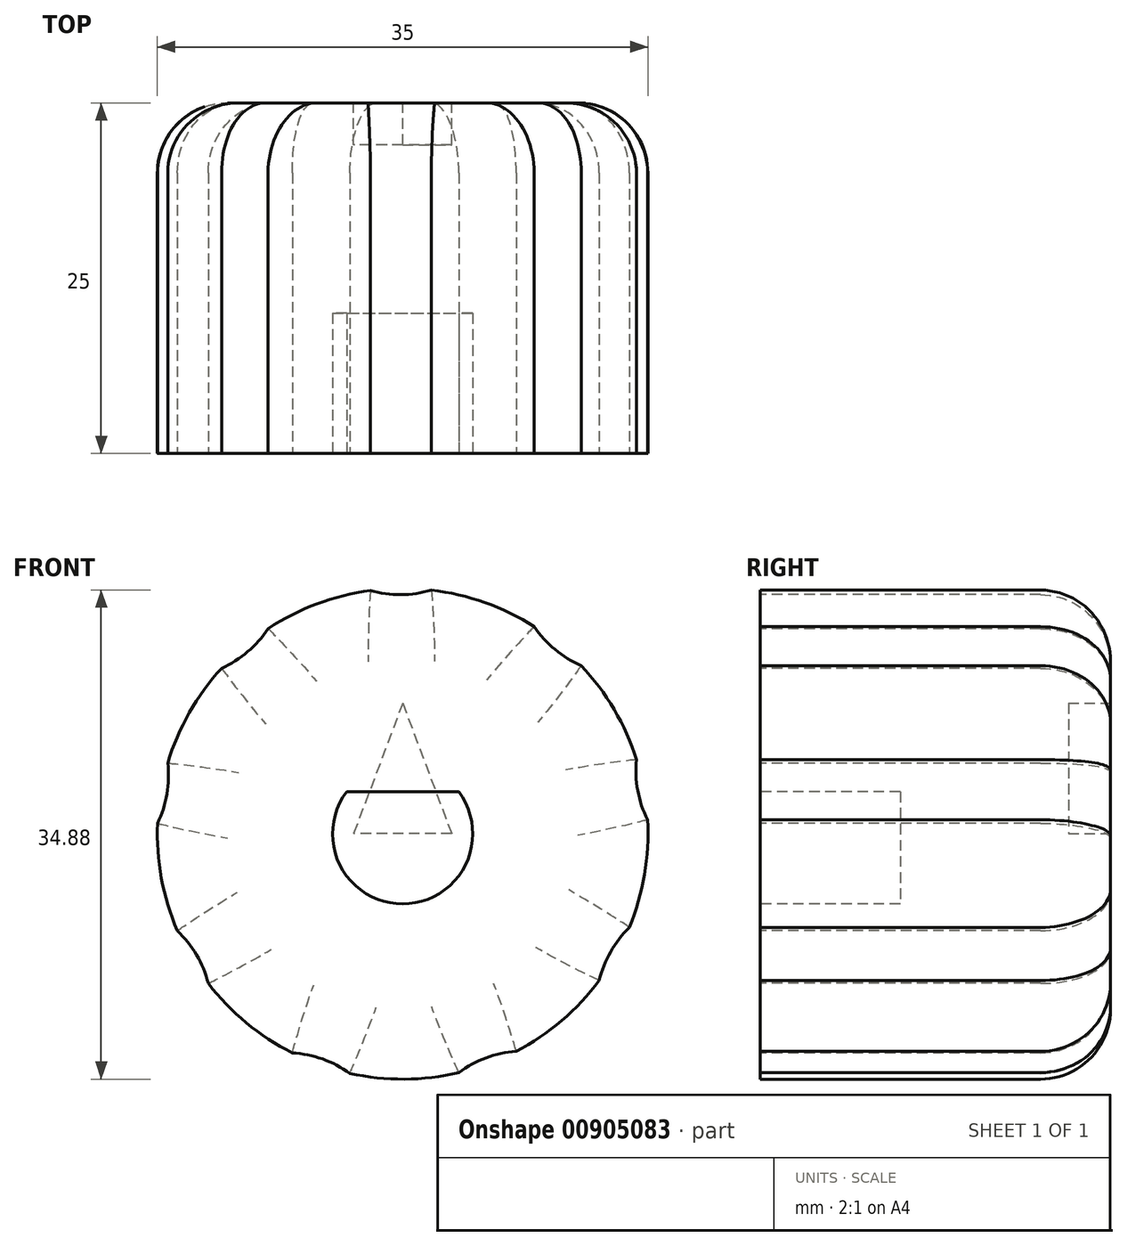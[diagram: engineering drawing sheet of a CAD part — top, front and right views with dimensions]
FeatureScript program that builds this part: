
annotation { "Feature Type Name" : "Feature", "Feature Type Description" : "" }
export const myFeature = defineFeature(function(context is Context, id is Id, definition is map)
    precondition{}
    {
        {
            var Q0;
            Q0=qCreatedBy(makeId("Front.planeOp"),FACE);
            var sketch = newSketch(context, id + "F0", { "sketchPlane" : qUnion([Q0])});
            skCircle(sketch, "E0", {"center": v(0, 0) * mm, "radius": 17.5 * mm});
            skCircle(sketch, "E1", {"center": v(0, 0) * mm, "radius": 5 * mm});
            skLineSegment(sketch, "E2", {"start": v(-4, 3) * mm, "end": v(4, 3) * mm});
            skLineSegment(sketch, "E3", {"start": v(-2.3, 17.35) * mm, "end": v(2.05, 17.38) * mm, "construction": true});
            skArc(sketch, "E4", {"start": v(-2.3, 17.35) * mm, "mid": v(-0.12, 17.05) * mm, "end": v(2.05, 17.38) * mm});
            skArc(sketch, "E5.1.0", {"start": v(-12.92, 11.8) * mm, "mid": v(-11.06, 12.98) * mm, "end": v(-9.6, 14.63) * mm});
            skArc(sketch, "E5.2.0", {"start": v(-17.48, 0.74) * mm, "mid": v(-16.82, 2.84) * mm, "end": v(-16.76, 5.04) * mm});
            skArc(sketch, "E5.3.0", {"start": v(-13.87, -10.67) * mm, "mid": v(-14.7, -8.63) * mm, "end": v(-16.08, -6.91) * mm});
            skArc(sketch, "E5.4.0", {"start": v(-3.77, -17.09) * mm, "mid": v(-5.72, -16.07) * mm, "end": v(-7.87, -15.63) * mm});
            skArc(sketch, "E5.5.0", {"start": v(8.1, -15.51) * mm, "mid": v(5.95, -15.98) * mm, "end": v(4.02, -17.03) * mm});
            skArc(sketch, "E5.6.0", {"start": v(16.18, -6.68) * mm, "mid": v(14.83, -8.42) * mm, "end": v(14.03, -10.47) * mm});
            skArc(sketch, "E5.7.0", {"start": v(16.68, 5.28) * mm, "mid": v(16.77, 3.08) * mm, "end": v(17.47, 1) * mm});
            skArc(sketch, "E5.8.0", {"start": v(9.39, 14.77) * mm, "mid": v(10.87, 13.14) * mm, "end": v(12.74, 12) * mm});
            skSolve(sketch);
        }
        {
            var Q0;
            {var subQ8=sQuery(id+"F0.wireOp",EDGE,"E4");Q0=makeQuery(id+"F0.imprint","IMPRINT",FACE,{"disambiguationData":[TD([[makeQuery(id+"F0.imprint","IMPRINT",EDGE,{"derivedFrom":subQ8}),-1.0]])]});}
            var Q1;
            {var subQ0=sQuery(id+"F0.wireOp",EDGE,"E2");Q1=makeQuery(id+"F0.imprint","IMPRINT",FACE,{"disambiguationData":[TD([[makeQuery(id+"F0.imprint","IMPRINT",EDGE,{"derivedFrom":subQ0}),1.0]])]});}
            var Q2;
            {var subQ0=sQuery(id+"F0.wireOp",EDGE,"E2");Q2=makeQuery(id+"F0.imprint","IMPRINT",FACE,{"disambiguationData":[TD([[makeQuery(id+"F0.imprint","IMPRINT",EDGE,{"derivedFrom":subQ0}),-1.0]])]});}
            extrude(context, id + "F1", {"entities" : qUnion([Q0, Q1, Q2]), "oppositeDirection" : true, "depth" : 25 * mm, "offsetDistance" : 25 * mm});
        }
        {
            var Q0;
            {var subQ0=sQuery(id+"F0.wireOp",EDGE,"E2");Q0=makeQuery(id+"F0.imprint","IMPRINT",FACE,{"disambiguationData":[TD([[makeQuery(id+"F0.imprint","IMPRINT",EDGE,{"derivedFrom":subQ0}),-1.0]])]});}
            extrude(context, id + "F2", {"entities" : qUnion([Q0]), "operationType" : NewBodyOperationType.REMOVE, "oppositeDirection" : true, "depth" : 10 * mm, "offsetDistance" : 25 * mm});
        }
        {
            var Q0;
            Q0=makeQuery(id+"F1.opExtrude","CAP_FACE",FACE,{"disambiguationData":[OSD([sQuery(id+"F0.wireOp",EDGE,"E0"),sQuery(id+"F0.wireOp",EDGE,"E4"),sQuery(id+"F0.wireOp",EDGE,"E5.1.0"),sQuery(id+"F0.wireOp",EDGE,"E5.2.0"),sQuery(id+"F0.wireOp",EDGE,"E5.3.0"),sQuery(id+"F0.wireOp",EDGE,"E5.4.0"),sQuery(id+"F0.wireOp",EDGE,"E5.5.0"),sQuery(id+"F0.wireOp",EDGE,"E5.6.0"),sQuery(id+"F0.wireOp",EDGE,"E5.7.0"),sQuery(id+"F0.wireOp",EDGE,"E5.8.0")])],"isStart":false});
            fillet(context, id + "F3", {"entities" : qUnion([Q0]), "radius" : 5 * mm, "tangentPropagation" : true, "allowEdgeOverflow" : false});
        }
        {
            var Q0;
            Q0=makeQuery(id+"F1.opExtrude","CAP_FACE",FACE,{"disambiguationData":[OSD([sQuery(id+"F0.wireOp",EDGE,"E0"),sQuery(id+"F0.wireOp",EDGE,"E4"),sQuery(id+"F0.wireOp",EDGE,"E5.1.0"),sQuery(id+"F0.wireOp",EDGE,"E5.2.0"),sQuery(id+"F0.wireOp",EDGE,"E5.3.0"),sQuery(id+"F0.wireOp",EDGE,"E5.4.0"),sQuery(id+"F0.wireOp",EDGE,"E5.5.0"),sQuery(id+"F0.wireOp",EDGE,"E5.6.0"),sQuery(id+"F0.wireOp",EDGE,"E5.7.0"),sQuery(id+"F0.wireOp",EDGE,"E5.8.0")])],"isStart":false});
            var sketch = newSketch(context, id + "F4", { "sketchPlane" : qUnion([Q0])});
            skLineSegment(sketch, "E6", {"start": v(0, 9.31) * mm, "end": v(0, -8.27) * mm, "construction": true});
            skLineSegment(sketch, "E7", {"start": v(0, 9.31) * mm, "end": v(3.5, 0) * mm});
            skLineSegment(sketch, "E8", {"start": v(3.5, 0) * mm, "end": v(0, 0) * mm});
            skLineSegment(sketch, "E9.MirrorCS", {"start": v(0, 9.31) * mm, "end": v(-3.5, 0) * mm});
            skLineSegment(sketch, "E10.MirrorCS", {"start": v(-3.5, 0) * mm, "end": v(0, 0) * mm});
            skSolve(sketch);
        }
        {
            var Q0;
            Q0=makeQuery(id+"F4.imprint","IMPRINT",FACE,{"disambiguationData":[TD([[makeQuery(id+"F4.imprint","IMPRINT",EDGE,{"derivedFrom":sQuery(id+"F4.wireOp",EDGE,"E7")}),-1.0]])]});
            extrude(context, id + "F5", {"entities" : qUnion([Q0]), "operationType" : NewBodyOperationType.REMOVE, "oppositeDirection" : true, "depth" : 3 * mm, "offsetDistance" : 25 * mm});
        }
    });
